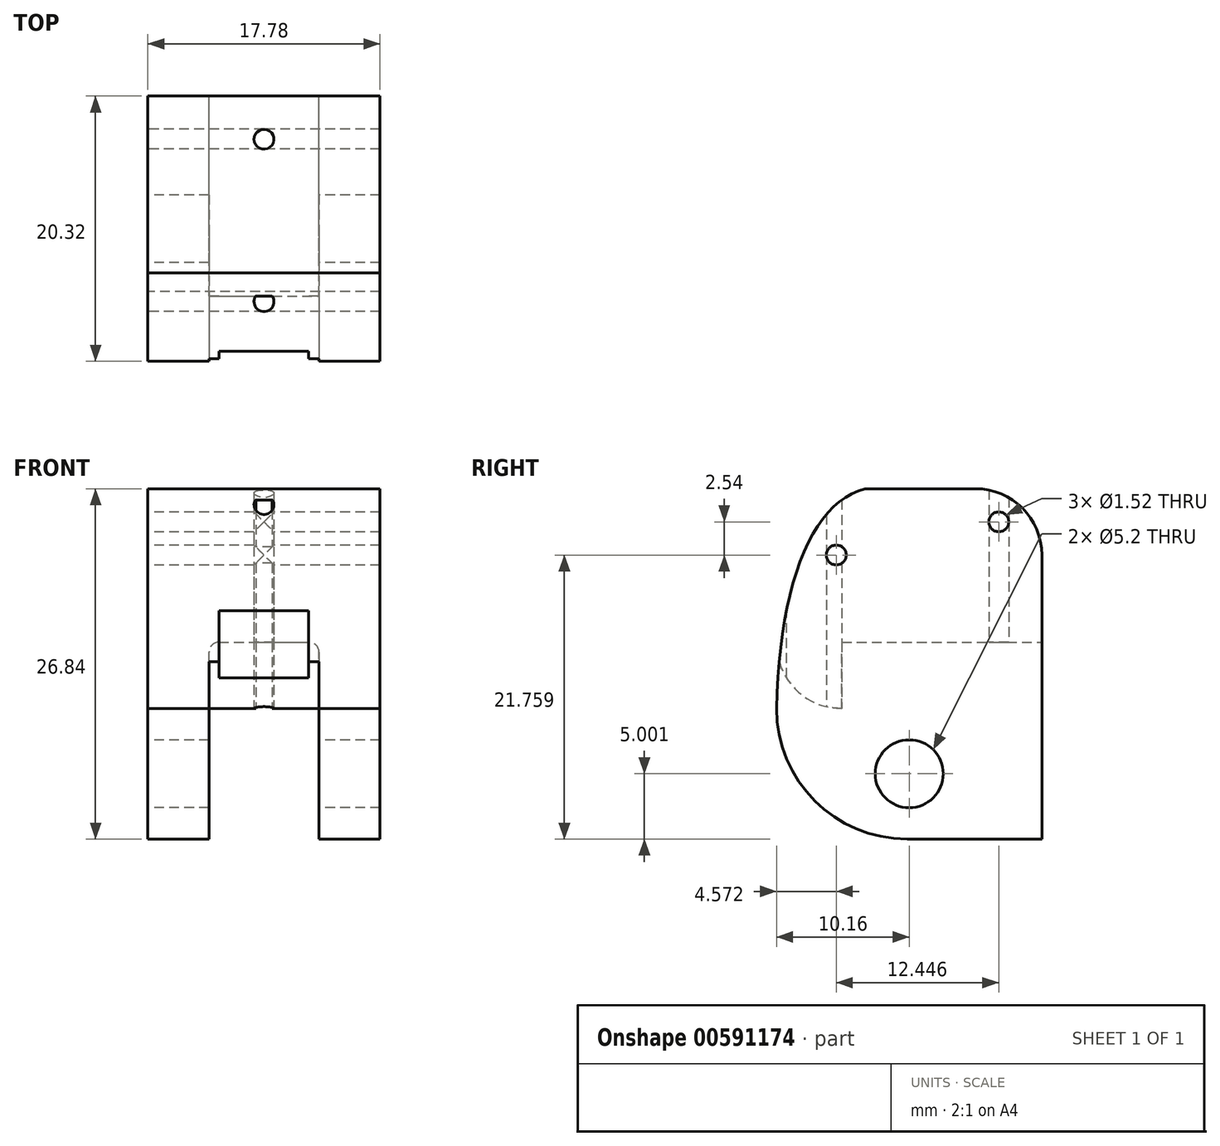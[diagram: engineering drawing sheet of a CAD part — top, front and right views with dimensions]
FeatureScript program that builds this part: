
annotation { "Feature Type Name" : "Feature", "Feature Type Description" : "" }
export const myFeature = defineFeature(function(context is Context, id is Id, definition is map)
    precondition{}
    {
        {
            var Q0;
            Q0=qCreatedBy(makeId("Front.planeOp"),FACE);
            var sketch = newSketch(context, id + "F0", { "sketchPlane" : qUnion([Q0])});
            skLineSegment(sketch, "E0.top", {"start": v(8.89, -13.42) * mm, "end": v(4.2, -13.42) * mm});
            skLineSegment(sketch, "E0.left", {"start": v(8.89, 13.42) * mm, "end": v(8.89, -13.42) * mm});
            skLineSegment(sketch, "E0.right", {"start": v(-8.9, 13.42) * mm, "end": v(-8.9, -13.42) * mm});
            skPoint(sketch, "E0.middle", {"position": v(0, 0) * mm});
            skLineSegment(sketch, "E1.left", {"start": v(4.2, -13.42) * mm, "end": v(4.2, -3.42) * mm});
            skLineSegment(sketch, "E2.trimOffspring", {"start": v(-4.21, -13.42) * mm, "end": v(-8.9, -13.42) * mm});
            skLineSegment(sketch, "E3", {"start": v(-8.9, 13.42) * mm, "end": v(8.89, 13.42) * mm});
            skLineSegment(sketch, "E4", {"start": v(-4.21, -13.42) * mm, "end": v(-4.21, -3.42) * mm});
            skLineSegment(sketch, "E5", {"start": v(-4.21, -3.42) * mm, "end": v(4.2, -3.42) * mm});
            skSolve(sketch);
        }
        {
            var Q0;
            Q0=makeQuery(id+"F0.imprint","IMPRINT",FACE,{"disambiguationData":[TD([[makeQuery(id+"F0.imprint","IMPRINT",EDGE,{"derivedFrom":sQuery(id+"F0.wireOp",EDGE,"E0.bottom")}),1.0]])]});
            var Q1;
            Q1=makeQuery(id+"F0.imprint","IMPRINT",FACE,{"disambiguationData":[TD([[makeQuery(id+"F0.imprint","IMPRINT",EDGE,{"derivedFrom":sQuery(id+"F0.wireOp",EDGE,"E0.top")}),-1.0]])]});
            extrude(context, id + "F1", {"entities" : qUnion([Q0, Q1]), "depth" : 20.32 * mm, "offsetDistance" : 25.4 * mm, "symmetric" : true});
        }
        {
            var Q0;
            Q0=makeQuery(id+"F1.opExtrude","SWEPT_FACE",FACE,{"disambiguationData":[OSD([sQuery(id+"F0.wireOp",EDGE,"E0.right")])]});
            var sketch = newSketch(context, id + "F2", { "sketchPlane" : qUnion([Q0])});
            skPoint(sketch, "E6.endSnap0", {"position": v(0, -13.42) * mm});
            skCircle(sketch, "E7", {"center": v(0, -8.42) * mm, "radius": 2.6 * mm});
            skSolve(sketch);
        }
        {
            var Q0;
            Q0=makeQuery(id+"F2.imprint","IMPRINT",FACE,{"disambiguationData":[TD([[makeQuery(id+"F2.imprint","IMPRINT",EDGE,{"derivedFrom":sQuery(id+"F2.wireOp",EDGE,"E7")}),1.0]])]});
            extrude(context, id + "F3", {"entities" : qUnion([Q0]), "operationType" : NewBodyOperationType.REMOVE, "endBound" : BoundingType.THROUGH_ALL, "oppositeDirection" : true, "depth" : 25.4 * mm, "offsetDistance" : 25.4 * mm});
        }
        {
            var Q0;
            Q0=makeQuery(id+"F1.opExtrude","CAP_EDGE",EDGE,{"disambiguationData":[OSD([sQuery(id+"F0.wireOp",EDGE,"E0.top")])],"isStart":false});
            var Q1;
            Q1=makeQuery(id+"F1.opExtrude","CAP_EDGE",EDGE,{"disambiguationData":[OSD([sQuery(id+"F0.wireOp",EDGE,"E2.trimOffspring")])],"isStart":false});
            fillet(context, id + "F4", {"entities" : qUnion([Q0, Q1]), "radius" : 10 * mm, "tangentPropagation" : true, "allowEdgeOverflow" : false});
        }
        {
            var Q0;
            Q0=makeQuery(id+"F1.opExtrude","CAP_EDGE",EDGE,{"disambiguationData":[OSD([sQuery(id+"F0.wireOp",EDGE,"n1KhcOkA-morR-dHWE-QHtQ-fdfn4GYgakT7"),sQuery(id+"F0.wireOp",EDGE,"so1H2Mnw-W18e-9x4z-PSc0-3TYgFntjAnIa")])],"isStart":false});
            var Q1;
            Q1=makeQuery(id+"F1.opExtrude","CAP_EDGE",EDGE,{"disambiguationData":[OSD([sQuery(id+"F0.wireOp",EDGE,"E5")])],"isStart":false});
            fillet(context, id + "F5", {"entities" : qUnion([Q0, Q1]), "radius" : 5 * mm, "tangentPropagation" : true, "allowEdgeOverflow" : false});
        }
        {
            var Q0;
            Q0=makeQuery(id+"F1.opExtrude","SWEPT_FACE",FACE,{"disambiguationData":[OSD([sQuery(id+"F0.wireOp",EDGE,"E0.right")])]});
            var sketch = newSketch(context, id + "F6", { "sketchPlane" : qUnion([Q0])});
            skLineSegment(sketch, "E8", {"start": v(10.16, 13.42) * mm, "end": v(10.16, -3.42) * mm});
            skEllipse(sketch, "E9", {"center": v(-7.08, -25.89) * mm, "majorRadius": 40.68 * mm, "minorRadius": 14.2 * mm, "majorAxis": v(0.26, 0.97)});
            skPoint(sketch, "E10", {"position": v(0, 13.42) * mm});
            skLineSegment(sketch, "E11", {"start": v(10.16, 13.42) * mm, "end": v(3.39, 13.42) * mm});
            skSolve(sketch);
        }
        {
            var Q0;
            {var subQ0=sQuery(id+"F6.wireOp",EDGE,"E8");Q0=makeQuery(id+"F6.imprint","IMPRINT",FACE,{"disambiguationData":[TD([[makeQuery(id+"F6.imprint","IMPRINT",EDGE,{"derivedFrom":subQ0}),-1.0]])]});}
            extrude(context, id + "F7", {"entities" : qUnion([Q0]), "operationType" : NewBodyOperationType.REMOVE, "endBound" : BoundingType.THROUGH_ALL, "oppositeDirection" : true, "depth" : 25.4 * mm, "offsetDistance" : 25.4 * mm});
        }
        {
            var Q0;
            Q0=makeQuery(id+"F1.opExtrude","CAP_EDGE",EDGE,{"disambiguationData":[OSD([sQuery(id+"F0.wireOp",EDGE,"E3")])],"isStart":true});
            fillet(context, id + "F8", {"entities" : qUnion([Q0]), "radius" : 5.08 * mm, "tangentPropagation" : true, "allowEdgeOverflow" : false});
        }
        {
            var Q0;
            Q0=makeQuery(id+"F1.opExtrude","SWEPT_FACE",FACE,{"disambiguationData":[OSD([sQuery(id+"F0.wireOp",EDGE,"E5")])]});
            var sketch = newSketch(context, id + "F9", { "sketchPlane" : qUnion([Q0])});
            skLineSegment(sketch, "E12", {"start": v(0, -10.16) * mm, "end": v(0, -7.62) * mm});
            skCircle(sketch, "E13", {"center": v(0, -6.86) * mm, "radius": 0.76 * mm});
            skCircle(sketch, "E14", {"center": v(0, 5.59) * mm, "radius": 0.76 * mm});
            skLineSegment(sketch, "E15", {"start": v(-8.9, 10.16) * mm, "end": v(8.89, 10.16) * mm});
            skLineSegment(sketch, "E16", {"start": v(0, 10.16) * mm, "end": v(0, 6.35) * mm});
            skSolve(sketch);
        }
        {
            var Q0;
            Q0=makeQuery(id+"F9.imprint","IMPRINT",FACE,{"disambiguationData":[TD([[makeQuery(id+"F9.imprint","IMPRINT",EDGE,{"derivedFrom":sQuery(id+"F9.wireOp",EDGE,"E14")}),1.0]])]});
            var Q1;
            Q1=makeQuery(id+"F9.imprint","IMPRINT",FACE,{"disambiguationData":[TD([[makeQuery(id+"F9.imprint","IMPRINT",EDGE,{"derivedFrom":sQuery(id+"F9.wireOp",EDGE,"E13")}),1.0]])]});
            var Q2;
            {var subQ0=sQuery(id+"F9.wireOp",EDGE,"E14");var subQ1=sQuery(id+"F0.wireOp",EDGE,"E5");var subQ2=makeQuery(id+"F5.opFillet","BLEND_EDGE",EDGE,{"blendedFrom":[makeQuery(id+"F1.opExtrude","CAP_EDGE",EDGE,{"disambiguationData":[OSD([subQ1])],"isStart":false}),makeQuery(id+"F1.opExtrude","SWEPT_FACE",FACE,{"disambiguationData":[OSD([subQ1])]})],"blendedInto":[makeQuery(id+"F1.opExtrude","SWEPT_FACE",FACE,{"disambiguationData":[OSD([subQ1])]})]});var subQ3=makeQuery(id+"F9.imprint","INTERSECT",VERTEX,{"disambiguationData":[OD(0.0)],"derivedFrom":[subQ2,subQ0]});Q2=makeQuery(id+"F9.imprint","IMPRINT",FACE,{"disambiguationData":[TD([[makeQuery(id+"F9.imprint","IMPRINT",EDGE,{"disambiguationData":[TD([[subQ3,-1.0]])],"derivedFrom":subQ0}),1.0]])]});}
            extrude(context, id + "F10", {"entities" : qUnion([Q0, Q1, Q2]), "operationType" : NewBodyOperationType.REMOVE, "endBound" : BoundingType.THROUGH_ALL, "oppositeDirection" : true, "depth" : 25.4 * mm, "offsetDistance" : 25.4 * mm});
        }
        {
            var Q0;
            Q0=makeQuery(id+"F1.opExtrude","SWEPT_FACE",FACE,{"disambiguationData":[OSD([sQuery(id+"F0.wireOp",EDGE,"E0.right")])]});
            var sketch = newSketch(context, id + "F11", { "sketchPlane" : qUnion([Q0])});
            skLineSegment(sketch, "E17", {"start": v(-7.62, 13.42) * mm, "end": v(-7.62, 10.88) * mm});
            skLineSegment(sketch, "E18", {"start": v(-7.62, 10.88) * mm, "end": v(-10.16, 10.88) * mm});
            skLineSegment(sketch, "E19", {"start": v(10.16, 8.34) * mm, "end": v(6.35, 8.34) * mm});
            skLineSegment(sketch, "E20", {"start": v(6.35, 8.34) * mm, "end": v(6.35, 13.42) * mm});
            skCircle(sketch, "E21", {"center": v(-6.86, 10.88) * mm, "radius": 0.76 * mm});
            skCircle(sketch, "E22", {"center": v(5.59, 8.34) * mm, "radius": 0.76 * mm});
            skLineSegment(sketch, "E23", {"start": v(-10.16, -13.42) * mm, "end": v(10.16, -13.42) * mm});
            skLineSegment(sketch, "E24", {"start": v(10.16, -13.42) * mm, "end": v(10.16, 8.34) * mm});
            skSolve(sketch);
        }
        {
            var Q0;
            Q0=makeQuery(id+"F11.imprint","IMPRINT",FACE,{"disambiguationData":[TD([[makeQuery(id+"F11.imprint","IMPRINT",EDGE,{"derivedFrom":sQuery(id+"F11.wireOp",EDGE,"E21")}),1.0]])]});
            var Q1;
            Q1=makeQuery(id+"F11.imprint","IMPRINT",FACE,{"disambiguationData":[TD([[makeQuery(id+"F11.imprint","IMPRINT",EDGE,{"derivedFrom":sQuery(id+"F11.wireOp",EDGE,"E22")}),1.0]])]});
            extrude(context, id + "F12", {"entities" : qUnion([Q0, Q1]), "operationType" : NewBodyOperationType.REMOVE, "endBound" : BoundingType.THROUGH_ALL, "oppositeDirection" : true, "depth" : 25.4 * mm, "offsetDistance" : 25.4 * mm});
        }
        {
            var Q0;
            {var subQ0=sQuery(id+"F0.wireOp",EDGE,"E2.trimOffspring");var subQ1=sQuery(id+"F0.wireOp",EDGE,"E0.right");var subQ2=sQuery(id+"F0.wireOp",EDGE,"E0.top");Q0=makeQuery(id+"F7.boolean.opBoolean","MERGE",EDGE,{"derivedFrom":[makeQuery(id+"F4.opFillet","BLEND_EDGE",EDGE,{"blendedFrom":[makeQuery(id+"F1.opExtrude","CAP_EDGE",EDGE,{"disambiguationData":[OSD([subQ2])],"isStart":false}),makeQuery(id+"F1.opExtrude","CAP_FACE",FACE,{"disambiguationData":[OSD([subQ2,sQuery(id+"F0.wireOp",EDGE,"E0.left"),subQ1,sQuery(id+"F0.wireOp",EDGE,"E1.left"),subQ0,sQuery(id+"F0.wireOp",EDGE,"E3"),sQuery(id+"F0.wireOp",EDGE,"E4"),sQuery(id+"F0.wireOp",EDGE,"E5")])],"isStart":false})],"blendedInto":[makeQuery(id+"F1.opExtrude","CAP_FACE",FACE,{"disambiguationData":[OSD([subQ2,sQuery(id+"F0.wireOp",EDGE,"E0.left"),subQ1,sQuery(id+"F0.wireOp",EDGE,"E1.left"),subQ0,sQuery(id+"F0.wireOp",EDGE,"E3"),sQuery(id+"F0.wireOp",EDGE,"E4"),sQuery(id+"F0.wireOp",EDGE,"E5")])],"isStart":false})]}),makeQuery(id+"F7.opExtrude","SWEPT_EDGE",EDGE,{"disambiguationData":[OSD([subQ1,subQ0,sQuery(id+"F6.wireOp",EDGE,"E8"),sQuery(id+"F6.wireOp",EDGE,"E9")])]})]});}
            cPlane(context, id + "F13", {"entities" : qUnion([Q0]), "cplaneType" : CPlaneType.LINE_ANGLE, "offset" : 25.4 * mm, "angle" : 0 * degree, "width" : 152.4 * mm, "height" : 152.4 * mm});
        }
        {
            var Q0;
            Q0=qCreatedBy(id+"F13.planeOp",FACE);
            var sketch = newSketch(context, id + "F14", { "sketchPlane" : qUnion([Q0])});
            skLineSegment(sketch, "E25", {"start": v(-8.9, 13.42) * mm, "end": v(8.89, 13.42) * mm});
            skLineSegment(sketch, "E26", {"start": v(0, 13.42) * mm, "end": v(0, 10.37) * mm});
            skCircle(sketch, "E27", {"center": v(0, 6.94) * mm, "radius": 3.43 * mm});
            skLineSegment(sketch, "E28", {"start": v(-3.43, 6.94) * mm, "end": v(0, 6.94) * mm});
            skLineSegment(sketch, "E29", {"start": v(3.43, 6.94) * mm, "end": v(0, 6.94) * mm});
            skLineSegment(sketch, "E30", {"start": v(-3.43, 6.94) * mm, "end": v(-3.43, -3.42) * mm});
            skLineSegment(sketch, "E31", {"start": v(-3.43, -3.42) * mm, "end": v(3.43, -3.42) * mm});
            skLineSegment(sketch, "E32", {"start": v(3.43, -3.42) * mm, "end": v(3.43, 6.94) * mm});
            skSolve(sketch);
        }
        {
            var Q0;
            Q0=makeQuery(id+"F1.opExtrude","CAP_FACE",FACE,{"disambiguationData":[OSD([sQuery(id+"F0.wireOp",EDGE,"E0.top"),sQuery(id+"F0.wireOp",EDGE,"E0.left"),sQuery(id+"F0.wireOp",EDGE,"E0.right"),sQuery(id+"F0.wireOp",EDGE,"E1.left"),sQuery(id+"F0.wireOp",EDGE,"E2.trimOffspring"),sQuery(id+"F0.wireOp",EDGE,"E3"),sQuery(id+"F0.wireOp",EDGE,"E4"),sQuery(id+"F0.wireOp",EDGE,"E5")])],"isStart":true});
            var sketch = newSketch(context, id + "F15", { "sketchPlane" : qUnion([Q0])});
            skLineSegment(sketch, "E33.top", {"start": v(0, 1.66) * mm, "end": v(3.45, 1.66) * mm});
            skLineSegment(sketch, "E33.right", {"start": v(4.21, -3.42) * mm, "end": v(4.21, 0.9) * mm});
            skLineSegment(sketch, "E34.bottom", {"start": v(0, 1.66) * mm, "end": v(0, 1.66) * mm});
            skLineSegment(sketch, "E35.bottom", {"start": v(0, 1.66) * mm, "end": v(-3.45, 1.66) * mm});
            skLineSegment(sketch, "E35.right", {"start": v(-4.2, 0.9) * mm, "end": v(-4.2, -3.42) * mm});
            skArc(sketch, "E36.filletArc", {"start": v(4.21, 0.9) * mm, "mid": v(3.99, 1.44) * mm, "end": v(3.45, 1.66) * mm});
            skArc(sketch, "E37.filletArc", {"start": v(-3.45, 1.66) * mm, "mid": v(-3.99, 1.44) * mm, "end": v(-4.2, 0.9) * mm});
            skLineSegment(sketch, "E38", {"start": v(0, 1.66) * mm, "end": v(0, -3.42) * mm});
            skLineSegment(sketch, "E39", {"start": v(-4.2, -3.42) * mm, "end": v(4.21, -3.42) * mm});
            skSolve(sketch);
        }
        {
            var Q0;
            {var subQ5=sQuery(id+"F15.wireOp",EDGE,"E35.bottom");Q0=makeQuery(id+"F15.imprint","IMPRINT",FACE,{"disambiguationData":[TD([[makeQuery(id+"F15.imprint","IMPRINT",EDGE,{"derivedFrom":subQ5}),1.0]])]});}
            var Q1;
            {var subQ5=sQuery(id+"F15.wireOp",EDGE,"E33.top");Q1=makeQuery(id+"F15.imprint","IMPRINT",FACE,{"disambiguationData":[TD([[makeQuery(id+"F15.imprint","IMPRINT",EDGE,{"derivedFrom":subQ5}),-1.0]])]});}
            var Q2;
            {var subQ0=sQuery(id+"F0.wireOp",EDGE,"E5");Q2=makeQuery(id+"F5.opFillet","BLEND_VERTEX",VERTEX,{"blendedFrom":[makeQuery(id+"F1.opExtrude","CAP_EDGE",EDGE,{"disambiguationData":[OSD([subQ0])],"isStart":false}),makeQuery(id+"F1.opExtrude","SWEPT_FACE",FACE,{"disambiguationData":[OSD([subQ0])]}),makeQuery(id+"F1.opExtrude","SWEPT_FACE",FACE,{"disambiguationData":[OSD([sQuery(id+"F0.wireOp",EDGE,"E4")])]})],"blendedInto":[makeQuery(id+"F1.opExtrude","SWEPT_FACE",FACE,{"disambiguationData":[OSD([subQ0])]}),makeQuery(id+"F1.opExtrude","SWEPT_FACE",FACE,{"disambiguationData":[OSD([sQuery(id+"F0.wireOp",EDGE,"E4")])]})]});}
            extrude(context, id + "F16", {"entities" : qUnion([Q0, Q1]), "operationType" : NewBodyOperationType.REMOVE, "endBound" : BoundingType.UP_TO_VERTEX, "oppositeDirection" : true, "depth" : 13.97 * mm, "endBoundEntityVertex" : qUnion([Q2]), "offsetDistance" : 25.4 * mm});
        }
        {
            var Q0;
            {var subQ3=sQuery(id+"F14.wireOp",EDGE,"E28");Q0=makeQuery(id+"F14.imprint","IMPRINT",FACE,{"disambiguationData":[TD([[makeQuery(id+"F14.imprint","IMPRINT",EDGE,{"derivedFrom":subQ3}),1.0]])]});}
            var Q1;
            {var subQ0=sQuery(id+"F14.wireOp",EDGE,"E28");Q1=makeQuery(id+"F14.imprint","IMPRINT",FACE,{"disambiguationData":[TD([[makeQuery(id+"F14.imprint","IMPRINT",EDGE,{"derivedFrom":subQ0}),-1.0]])]});}
            var Q2;
            {var subQ0=sQuery(id+"F14.wireOp",EDGE,"E30");Q2=makeQuery(id+"F14.imprint","IMPRINT",FACE,{"disambiguationData":[TD([[makeQuery(id+"F14.imprint","IMPRINT",EDGE,{"derivedFrom":subQ0}),1.0]])]});}
            extrude(context, id + "F17", {"entities" : qUnion([Q0, Q1, Q2]), "operationType" : NewBodyOperationType.REMOVE, "oppositeDirection" : true, "depth" : 0.76 * mm, "offsetDistance" : 25.4 * mm});
        }
    });
